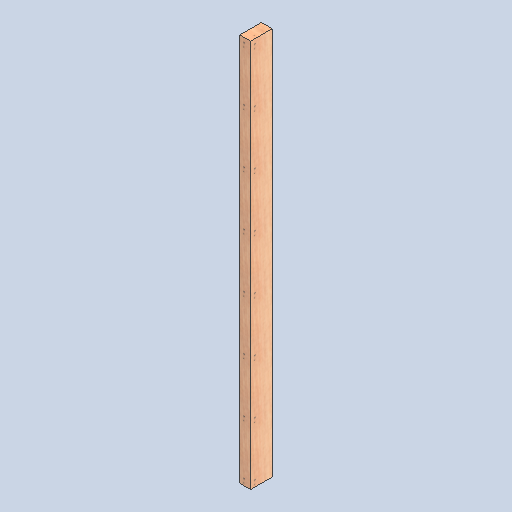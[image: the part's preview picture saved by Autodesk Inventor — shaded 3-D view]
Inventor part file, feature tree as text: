
AUTODESK INVENTOR PART (.ipt)
format: ipt  version: 2025 (Build 290162000, 162)  size: 116,736 bytes
history: native  units: in
note: dims shown in document units (in); Inventor stores cm internally (conversion verified against a paired STEP export)
features: extrude x1, sketch x1
ambient origin geometry x8: Origin, YZ Plane, XZ Plane, XY Plane, X Axis, Y Axis, Z Axis, Center Point
bodies: Solid1 (feature_tree)
feature tree (2):
  extrude  "Extrusion1"  Depth=4.0in
  sketch  "Sketch1"  dims[d0=2.0in d1=4.0in d2=72.0in d3=0.0in d5=0.5in d6=0.0344in d7=0.5in d8=0.0344in]
